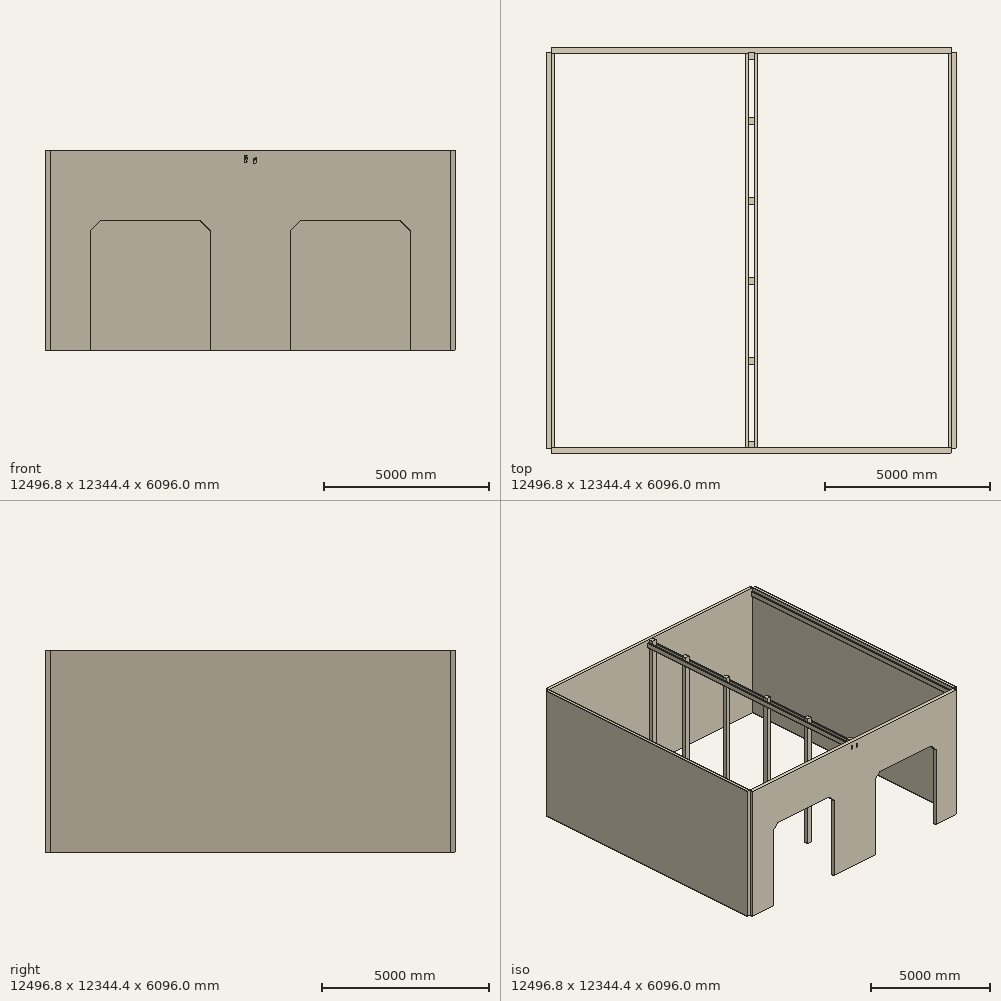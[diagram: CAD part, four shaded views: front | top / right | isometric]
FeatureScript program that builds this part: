
annotation { "Feature Type Name" : "Feature", "Feature Type Description" : "" }
export const myFeature = defineFeature(function(context is Context, id is Id, definition is map)
    precondition{}
    {
        {
            var Q0;
            Q0=qCreatedBy(makeId("Front.planeOp"),FACE);
            var sketch = newSketch(context, id + "F0", { "sketchPlane" : qUnion([Q0])});
            skLineSegment(sketch, "E0", {"start": v(0, 0) * mm, "end": v(-1219.2, 0) * mm});
            skLineSegment(sketch, "E1", {"start": v(-1219.2, 0) * mm, "end": v(-1219.2, 3657.6) * mm});
            skLineSegment(sketch, "E2", {"start": v(-4876.8, 3657.6) * mm, "end": v(-4876.8, 0) * mm});
            skLineSegment(sketch, "E3", {"start": v(0, 0) * mm, "end": v(0, 6096) * mm});
            skLineSegment(sketch, "E4", {"start": v(0, 6096) * mm, "end": v(-12192, 6096) * mm});
            skLineSegment(sketch, "E5", {"start": v(-12192, 6096) * mm, "end": v(-12192, 0) * mm});
            skLineSegment(sketch, "E6", {"start": v(-12192, 0) * mm, "end": v(-10972.8, 0) * mm});
            skLineSegment(sketch, "E7", {"start": v(-10972.8, 0) * mm, "end": v(-10972.8, 3657.6) * mm});
            skLineSegment(sketch, "E8", {"start": v(-7315.2, 3657.6) * mm, "end": v(-7315.2, 0) * mm});
            skLineSegment(sketch, "E9", {"start": v(-7315.2, 0) * mm, "end": v(-4876.8, 0) * mm});
            skLineSegment(sketch, "E10", {"start": v(-10668, 3962.4) * mm, "end": v(-10972.8, 3657.6) * mm});
            skLineSegment(sketch, "E11", {"start": v(-7620, 3962.4) * mm, "end": v(-7315.2, 3657.6) * mm});
            skLineSegment(sketch, "E12", {"start": v(-10668, 3962.4) * mm, "end": v(-7620, 3962.4) * mm});
            skLineSegment(sketch, "E13", {"start": v(-4572, 3962.4) * mm, "end": v(-4876.8, 3657.6) * mm});
            skLineSegment(sketch, "E14", {"start": v(-1524, 3962.4) * mm, "end": v(-1219.2, 3657.6) * mm});
            skLineSegment(sketch, "E15", {"start": v(-4572, 3962.4) * mm, "end": v(-1524, 3962.4) * mm});
            skSolve(sketch);
        }
        {
            var Q0;
            Q0 = qSketchRegion(id + "F0", true);
            extrude(context, id + "F1", {"entities" : qUnion([Q0]), "depth" : 152.4 * mm});
        }
        {
            var Q0;
            Q0=makeQuery(id+"F1.opExtrude","SWEPT_FACE",FACE,{"disambiguationData":[OSD([sQuery(id+"F0.wireOp",EDGE,"E3")])]});
            var sketch = newSketch(context, id + "F2", { "sketchPlane" : qUnion([Q0])});
            skLineSegment(sketch, "E16.bottom", {"start": v(-152.4, 0) * mm, "end": v(12039.6, 0) * mm});
            skLineSegment(sketch, "E16.top", {"start": v(-152.4, 6096) * mm, "end": v(12039.6, 6096) * mm});
            skLineSegment(sketch, "E16.left", {"start": v(-152.4, 0) * mm, "end": v(-152.4, 6096) * mm});
            skLineSegment(sketch, "E16.right", {"start": v(12039.6, 0) * mm, "end": v(12039.6, 6096) * mm});
            skSolve(sketch);
        }
        {
            var Q0;
            {var subQ2=sQuery(id+"F2.wireOp",EDGE,"E16.right");Q0=makeQuery(id+"F2.imprint","IMPRINT",FACE,{"disambiguationData":[TD([[makeQuery(id+"F2.imprint","IMPRINT",EDGE,{"derivedFrom":subQ2}),1.0]])]});}
            extrude(context, id + "F3", {"entities" : qUnion([Q0]), "depth" : 152.4 * mm});
        }
        {
            var Q0;
            Q0=makeQuery(id+"F1.opExtrude","SWEPT_FACE",FACE,{"disambiguationData":[OSD([sQuery(id+"F0.wireOp",EDGE,"E5")])]});
            var sketch = newSketch(context, id + "F4", { "sketchPlane" : qUnion([Q0])});
            skLineSegment(sketch, "E17.bottom", {"start": v(152.4, 0) * mm, "end": v(-12039.6, 0) * mm});
            skLineSegment(sketch, "E17.top", {"start": v(152.4, 6096) * mm, "end": v(-12039.6, 6096) * mm});
            skLineSegment(sketch, "E17.left", {"start": v(152.4, 0) * mm, "end": v(152.4, 6096) * mm});
            skLineSegment(sketch, "E17.right", {"start": v(-12039.6, 0) * mm, "end": v(-12039.6, 6096) * mm});
            skSolve(sketch);
        }
        {
            var Q0;
            {var subQ2=sQuery(id+"F4.wireOp",EDGE,"E17.right");Q0=makeQuery(id+"F4.imprint","IMPRINT",FACE,{"disambiguationData":[TD([[makeQuery(id+"F4.imprint","IMPRINT",EDGE,{"derivedFrom":subQ2}),-1.0]])]});}
            extrude(context, id + "F5", {"entities" : qUnion([Q0]), "depth" : 152.4 * mm});
        }
        {
            var Q0;
            Q0=makeQuery(id+"F3.opExtrude","SWEPT_FACE",FACE,{"disambiguationData":[OSD([sQuery(id+"F2.wireOp",EDGE,"E16.right")])]});
            var sketch = newSketch(context, id + "F6", { "sketchPlane" : qUnion([Q0])});
            skLineSegment(sketch, "E18.bottom", {"start": v(0, 6096) * mm, "end": v(12192, 6096) * mm});
            skLineSegment(sketch, "E18.top", {"start": v(0, 0) * mm, "end": v(12192, 0) * mm});
            skLineSegment(sketch, "E18.left", {"start": v(0, 6096) * mm, "end": v(0, 0) * mm});
            skLineSegment(sketch, "E18.right", {"start": v(12192, 6096) * mm, "end": v(12192, 0) * mm});
            skSolve(sketch);
        }
        {
            var Q0;
            Q0 = qSketchRegion(id + "F6", true);
            extrude(context, id + "F7", {"entities" : qUnion([Q0]), "depth" : 152.4 * mm});
        }
        {
            var Q0;
            Q0=makeQuery(id+"F5.opExtrude","SWEPT_FACE",FACE,{"disambiguationData":[OSD([sQuery(id+"F4.wireOp",EDGE,"E17.bottom")])]});
            var sketch = newSketch(context, id + "F8", { "sketchPlane" : qUnion([Q0])});
            skLineSegment(sketch, "E19.bottom", {"start": v(-6096, 0) * mm, "end": v(-5994.4, 0) * mm});
            skLineSegment(sketch, "E19.top", {"start": v(-6096, -203.2) * mm, "end": v(-5994.4, -203.2) * mm});
            skLineSegment(sketch, "E19.right", {"start": v(-5994.4, 0) * mm, "end": v(-5994.4, -203.2) * mm});
            skLineSegment(sketch, "E20.bottom", {"start": v(-6096, 0) * mm, "end": v(-6197.6, 0) * mm});
            skLineSegment(sketch, "E20.top", {"start": v(-6096, -203.2) * mm, "end": v(-6197.6, -203.2) * mm});
            skLineSegment(sketch, "E20.right", {"start": v(-6197.6, 0) * mm, "end": v(-6197.6, -203.2) * mm});
            skLineSegment(sketch, "E21.bottom", {"start": v(-5994.4, -9855.2) * mm, "end": v(-6197.6, -9855.2) * mm});
            skLineSegment(sketch, "E21.top", {"start": v(-5994.4, -10058.4) * mm, "end": v(-6197.6, -10058.4) * mm});
            skLineSegment(sketch, "E21.left", {"start": v(-5994.4, -9855.2) * mm, "end": v(-5994.4, -10058.4) * mm});
            skLineSegment(sketch, "E21.right", {"start": v(-6197.6, -9855.2) * mm, "end": v(-6197.6, -10058.4) * mm});
            skPoint(sketch, "E21.middle", {"position": v(-6096, -9956.8) * mm});
            skLineSegment(sketch, "E22.bottom", {"start": v(-5994.4, -7416.8) * mm, "end": v(-6197.6, -7416.8) * mm});
            skLineSegment(sketch, "E22.top", {"start": v(-5994.4, -7620) * mm, "end": v(-6197.6, -7620) * mm});
            skLineSegment(sketch, "E22.left", {"start": v(-5994.4, -7416.8) * mm, "end": v(-5994.4, -7620) * mm});
            skLineSegment(sketch, "E22.right", {"start": v(-6197.6, -7416.8) * mm, "end": v(-6197.6, -7620) * mm});
            skPoint(sketch, "E22.middle", {"position": v(-6096, -7518.4) * mm});
            skLineSegment(sketch, "E23.bottom", {"start": v(-5994.4, -4978.4) * mm, "end": v(-6197.6, -4978.4) * mm});
            skLineSegment(sketch, "E23.top", {"start": v(-5994.4, -5181.6) * mm, "end": v(-6197.6, -5181.6) * mm});
            skLineSegment(sketch, "E23.left", {"start": v(-5994.4, -4978.4) * mm, "end": v(-5994.4, -5181.6) * mm});
            skLineSegment(sketch, "E23.right", {"start": v(-6197.6, -4978.4) * mm, "end": v(-6197.6, -5181.6) * mm});
            skPoint(sketch, "E23.middle", {"position": v(-6096, -5080) * mm});
            skLineSegment(sketch, "E24.bottom", {"start": v(-6197.6, -2540) * mm, "end": v(-5994.4, -2540) * mm});
            skLineSegment(sketch, "E24.top", {"start": v(-6197.6, -2743.2) * mm, "end": v(-5994.4, -2743.2) * mm});
            skLineSegment(sketch, "E24.left", {"start": v(-6197.6, -2540) * mm, "end": v(-6197.6, -2743.2) * mm});
            skLineSegment(sketch, "E24.right", {"start": v(-5994.4, -2540) * mm, "end": v(-5994.4, -2743.2) * mm});
            skPoint(sketch, "E24.middle", {"position": v(-6096, -2641.6) * mm});
            skLineSegment(sketch, "E25.bottom", {"start": v(-6096, -12039.6) * mm, "end": v(-5994.4, -12039.6) * mm});
            skLineSegment(sketch, "E25.top", {"start": v(-6096, -11836.4) * mm, "end": v(-5994.4, -11836.4) * mm});
            skLineSegment(sketch, "E25.right", {"start": v(-5994.4, -12039.6) * mm, "end": v(-5994.4, -11836.4) * mm});
            skLineSegment(sketch, "E26.bottom", {"start": v(-6096, -12039.6) * mm, "end": v(-6197.6, -12039.6) * mm});
            skLineSegment(sketch, "E26.top", {"start": v(-6096, -11836.4) * mm, "end": v(-6197.6, -11836.4) * mm});
            skLineSegment(sketch, "E26.right", {"start": v(-6197.6, -12039.6) * mm, "end": v(-6197.6, -11836.4) * mm});
            skSolve(sketch);
        }
        {
            var Q0;
            Q0 = qSketchRegion(id + "F8", true);
            extrude(context, id + "F9", {"entities" : qUnion([Q0]), "oppositeDirection" : true, "depth" : 6096 * mm});
        }
        {
            var Q0;
            Q0=makeQuery(id+"F9.opExtrude","SWEPT_FACE",FACE,{"disambiguationData":[OSD([sQuery(id+"F8.wireOp",EDGE,"E25.right")])]});
            var sketch = newSketch(context, id + "F10", { "sketchPlane" : qUnion([Q0])});
            skLineSegment(sketch, "E27.bottom", {"start": v(12039.6, 5892.8) * mm, "end": v(-152.4, 5892.8) * mm});
            skLineSegment(sketch, "E27.top", {"start": v(12039.6, 5689.6) * mm, "end": v(-152.4, 5689.6) * mm});
            skLineSegment(sketch, "E27.left", {"start": v(12039.6, 5892.8) * mm, "end": v(12039.6, 5689.6) * mm});
            skLineSegment(sketch, "E27.right", {"start": v(-152.4, 5892.8) * mm, "end": v(-152.4, 5689.6) * mm});
            skSolve(sketch);
        }
        {
            var Q0;
            Q0 = qSketchRegion(id + "F10", true);
            extrude(context, id + "F11", {"entities" : qUnion([Q0]), "depth" : 76.2 * mm});
        }
        {
            var Q0;
            Q0=makeQuery(id+"F9.opExtrude","SWEPT_FACE",FACE,{"disambiguationData":[OSD([sQuery(id+"F8.wireOp",EDGE,"E26.right")])]});
            var sketch = newSketch(context, id + "F12", { "sketchPlane" : qUnion([Q0])});
            skLineSegment(sketch, "E28", {"start": v(-12039.6, 6096) * mm, "end": v(-12039.6, 5943.6) * mm});
            skLineSegment(sketch, "E29.bottom", {"start": v(-12039.6, 5943.6) * mm, "end": v(152.4, 5943.6) * mm});
            skLineSegment(sketch, "E29.top", {"start": v(-12039.6, 5740.4) * mm, "end": v(152.4, 5740.4) * mm});
            skLineSegment(sketch, "E29.left", {"start": v(-12039.6, 5943.6) * mm, "end": v(-12039.6, 5740.4) * mm});
            skLineSegment(sketch, "E29.right", {"start": v(152.4, 5943.6) * mm, "end": v(152.4, 5740.4) * mm});
            skSolve(sketch);
        }
        {
            var Q0;
            Q0 = qSketchRegion(id + "F12", true);
            extrude(context, id + "F13", {"entities" : qUnion([Q0]), "depth" : 76.2 * mm});
        }
        {
            var Q0;
            Q0=makeQuery(id+"F5.opExtrude","CAP_FACE",FACE,{"disambiguationData":[OSD([sQuery(id+"F0.wireOp",EDGE,"E5"),sQuery(id+"F4.wireOp",EDGE,"E17.bottom"),sQuery(id+"F4.wireOp",EDGE,"E17.top"),sQuery(id+"F4.wireOp",EDGE,"E17.right")])],"isStart":true});
            var sketch = newSketch(context, id + "F14", { "sketchPlane" : qUnion([Q0])});
            skLineSegment(sketch, "E30", {"start": v(12039.6, 5943.6) * mm, "end": v(-152.4, 5943.6) * mm});
            skLineSegment(sketch, "E31", {"start": v(-152.4, 5943.6) * mm, "end": v(-152.4, 5740.4) * mm});
            skLineSegment(sketch, "E32", {"start": v(-152.4, 5740.4) * mm, "end": v(12039.6, 5740.4) * mm});
            skLineSegment(sketch, "E33", {"start": v(12039.6, 5740.4) * mm, "end": v(12039.6, 5943.6) * mm});
            skSolve(sketch);
        }
        {
            var Q0;
            {var subQ0=sQuery(id+"F14.wireOp",EDGE,"E33");Q0=makeQuery(id+"F14.imprint","IMPRINT",FACE,{"disambiguationData":[TD([[makeQuery(id+"F14.imprint","IMPRINT",EDGE,{"derivedFrom":subQ0}),1.0]])]});}
            extrude(context, id + "F15", {"entities" : qUnion([Q0]), "depth" : 76.2 * mm});
        }
        {
            var Q0;
            Q0=makeQuery(id+"F3.opExtrude","CAP_FACE",FACE,{"disambiguationData":[OSD([sQuery(id+"F0.wireOp",EDGE,"E3"),sQuery(id+"F2.wireOp",EDGE,"E16.bottom"),sQuery(id+"F2.wireOp",EDGE,"E16.top"),sQuery(id+"F2.wireOp",EDGE,"E16.right")])],"isStart":true});
            var sketch = newSketch(context, id + "F16", { "sketchPlane" : qUnion([Q0])});
            skLineSegment(sketch, "E34", {"start": v(-12039.6, 5943.6) * mm, "end": v(152.4, 5943.6) * mm});
            skLineSegment(sketch, "E35", {"start": v(152.4, 5943.6) * mm, "end": v(152.4, 5740.4) * mm});
            skLineSegment(sketch, "E36", {"start": v(152.4, 5740.4) * mm, "end": v(-12039.6, 5740.4) * mm});
            skLineSegment(sketch, "E37", {"start": v(-12039.6, 5740.4) * mm, "end": v(-12039.6, 5943.6) * mm});
            skSolve(sketch);
        }
        {
            var Q0;
            {var subQ0=sQuery(id+"F16.wireOp",EDGE,"E37");Q0=makeQuery(id+"F16.imprint","IMPRINT",FACE,{"disambiguationData":[TD([[makeQuery(id+"F16.imprint","IMPRINT",EDGE,{"derivedFrom":subQ0}),-1.0]])]});}
            extrude(context, id + "F17", {"entities" : qUnion([Q0]), "depth" : 76.2 * mm});
        }
    });
